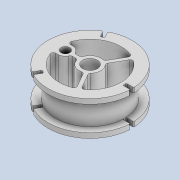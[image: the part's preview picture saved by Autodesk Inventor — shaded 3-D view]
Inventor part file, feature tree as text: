
AUTODESK INVENTOR PART (.ipt)
format: ipt  version: 2020 (Build 240168000, 168)  size: 399,360 bytes
history: native  units: mm
features: extrude x6, sketch x6, fillet x4, projected_geometry x4, pattern_circular x1
ambient origin geometry x8: Origin, YZ Plane, XZ Plane, XY Plane, X Axis, Y Axis, Z Axis, Center Point
bodies: Solid1 (feature_tree)
feature tree (21):
  extrude  "Extrusion1"  Depth=3.0mm
  extrude  "Extrusion2"  Depth=0.7mm
  extrude  "Extrusion3"  Depth=0.7mm
  extrude  "Extrusion4"  Depth=5.0mm
  extrude  "Extrusion5"  Depth=7.0mm TaperAngle=0.0deg
  pattern_circular  "Circular Pattern1"  [2 undecoded]
  fillet  "Fillet1"  Radius=1.5mm
  fillet  "Fillet2"  Radius=1.0mm
  extrude  "Extrusion6"  Depth=0.5mm TaperAngle=0.0deg
  fillet  "Fillet3"  [1 undecoded]
  fillet  "Fillet4"  Radius=3.0mm
  sketch  "Sketch1"  dims[d0=14.0mm d1=3.0mm]
  sketch  "Sketch2"  dims[d2=0.7mm d3=0.7mm]
  projected_geometry  "Projected Loop1"
  sketch  "Sketch3"  dims[d4=3.5mm d5=0.7mm]
  projected_geometry  "Projected Loop2"
  sketch  "Sketch4"  dims[d6=30.0mm d8=360.0deg d10=5.0mm]
  projected_geometry  "Projected Loop3"
  sketch  "Sketch5"  dims[d11=3.0mm d12=7.0mm d13=0.0mm]
  projected_geometry  "Projected Loop4"
  sketch  "Sketch6"  dims[d14=1.8mm d15=19.5mm d16=0.0mm d17=1.5mm d18=1.0mm d19=0.0mm d20=1.0mm d21=0.0mm d22=60.0deg d23=3.0mm d24=0.7mm d25=20.0mm d26=0.0mm d27=30.0mm d28=360.0deg d30=0.2mm d31=0.5mm d32=5.5mm d33=2.0mm d34=0.0mm d35=0.5mm d36=0.5mm]
note: 3 required parameter values undecoded (feature->parameter linkage not recoverable at this tier; creation-order binding heuristic only, values carry confidence <= 0.55)
